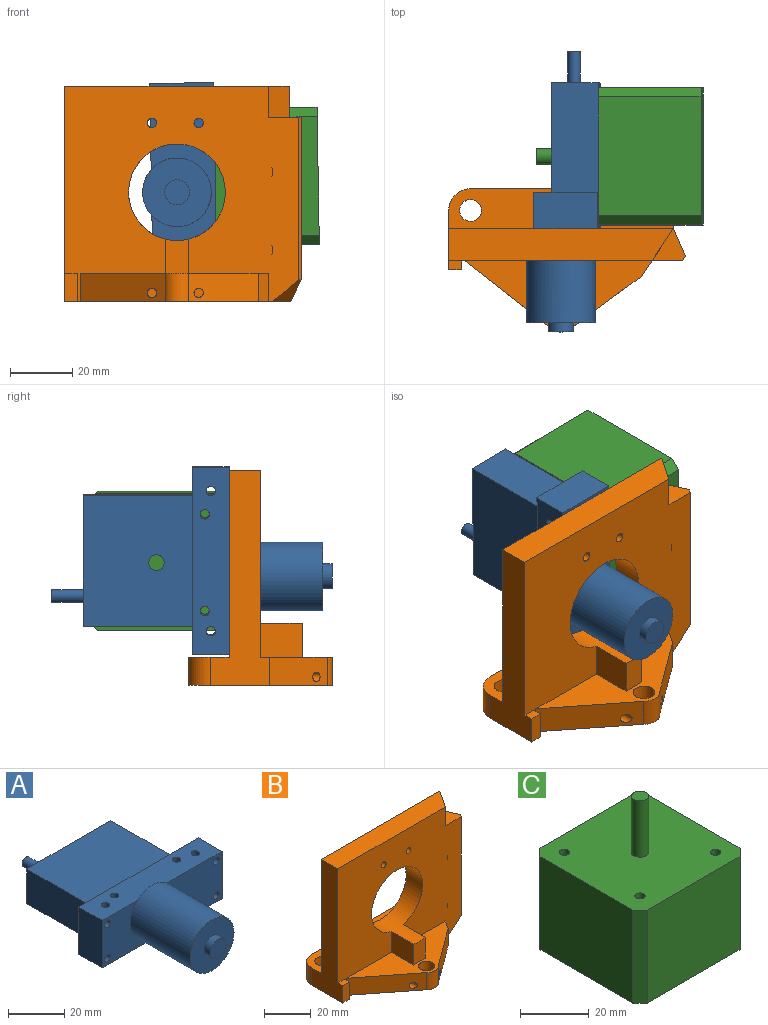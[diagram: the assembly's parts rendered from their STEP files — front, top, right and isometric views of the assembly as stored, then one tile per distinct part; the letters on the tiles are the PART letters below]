
ASSEMBLY  parts=3 mates=2
PART A: 25 faces, bbox 60x89.8x23.3 mm
  f0: plane 20.5x11.8mm, normal (1,0,0), area 241.9mm2, adj f1,f7,f8,f9
  f1: plane 60x20.5mm, normal (0,1,0), area 571.7mm2, adj f0,f2,f8,f9,f10,f11,f12,f13
  f2: plane 20.5x11.8mm, normal (-1,0,0), area 241.9mm2, adj f1,f7,f8,f9
  f3: cylinder r=1.5mm len=20.5mm, axis (0,0,-1), area 193.2mm2, adj f8,f9
  f4: cylinder r=1.5mm len=20.5mm, axis (0,0,-1), area 193.2mm2, adj f8,f9
  f5: cylinder r=1.5mm len=20.5mm, axis (0,0,-1), area 193.2mm2, adj f8,f9
  f6: cylinder r=1.5mm len=20.5mm, axis (0,0,-1), area 193.2mm2, adj f8,f9
  f7: plane 60x20.5mm, normal (0,-1,0), area 850.3mm2, adj f0,f2,f8,f9,f10,f11,f12,f13
  f8: plane 60x11.8mm, normal (0,0,1), area 679.7mm2, adj f0,f1,f2,f3,f4,f5,f6,f7
  f9: plane 60x46.8mm, normal (0,0,-1), area 2149.7mm2, adj f0,f1,f2,f3,f4,f5,f6,f7
  f10: cylinder r=1.5mm len=11.8mm, axis (0,1,0), area 111.2mm2, adj f1,f7
  f11: cylinder r=1.5mm len=11.8mm, axis (0,1,0), area 111.2mm2, adj f1,f7
  f12: cylinder r=1.5mm len=11.8mm, axis (0,1,0), area 111.2mm2, adj f1,f7
  f13: cylinder r=1.5mm len=11.8mm, axis (0,1,0), area 111.2mm2, adj f1,f7
  f14: plane 14.75x2.84mm, normal (0,1,0), area 28.7mm2, adj f8,f15
  f15: cylinder r=11mm len=30mm, axis (0,1,0), area 2073.5mm2, adj f7,f14,f16
  f16: plane 22x22mm, normal (0,-1,0), area 329.9mm2, adj f15,f17
  f17: cylinder r=4mm len=8mm, axis (0,1,0), area 75.4mm2, adj f16,f18
  f18: plane 8x8mm, normal (0,-1,0), area 50.3mm2, adj f17
  f19: plane 35x15mm, normal (1,0,0), area 525mm2, adj f1,f9,f21,f22
  f20: plane 35x15mm, normal (-1,0,0), area 525mm2, adj f1,f9,f21,f22
  f21: plane 42x35mm, normal (0,0,1), area 1470mm2, adj f1,f19,f20,f22
  f22: plane 42x15mm, normal (0,1,0), area 617.4mm2, adj f9,f19,f20,f21,f23
  f23: cylinder r=2mm len=10mm, axis (0,-1,0), area 125.7mm2, adj f22,f24
  f24: plane 4x4mm, normal (0,1,0), area 12.6mm2, adj f23
PART B: 47 faces, bbox 76.3x46.5x69.5 mm
  f0: plane 60.32x23mm, normal (0,0,1), area 624.9mm2, adj f1,f2,f11,f12,f13,f17,f35,f36
  f1: plane 75.19x69.19mm, normal (0,-1,0), area 3624.5mm2, adj f0,f2,f3,f8,f10,f11,f14,f19
  f2: plane 9x4.97mm, normal (0.83,-0.56,0), area 53.8mm2, adj f0,f1,f13,f19
  f3: plane 4x3mm, normal (0,0,1), area 12mm2, adj f1,f8,f9,f10
  f4: plane 72x13mm, normal (0,0,1), area 838mm2, adj f5,f6,f7,f8,f15,f16,f18,f25
  f5: cylinder r=7mm len=9mm, axis (0,0,-1), area 99mm2, adj f4,f6,f18,f19
  f6: plane 58x9mm, normal (0,1,0), area 522mm2, adj f4,f5,f7,f19
  f7: cylinder r=7mm len=9mm, axis (0,0,-1), area 99mm2, adj f4,f6,f8,f19
  f8: plane 69x19mm, normal (-1,0,0), area 771mm2, adj f1,f3,f4,f7,f9,f19,f25,f26
  f9: plane 9x4mm, normal (0,-1,0), area 36mm2, adj f3,f8,f10,f19
  f10: plane 9x3mm, normal (1,0,0), area 27mm2, adj f1,f3,f9,f19
  f11: plane 27.86x21.93mm, normal (-0.62,-0.79,0), area 303.8mm2, adj f0,f1,f12,f19,f39
  f12: cylinder r=5mm len=9mm, axis (0,0,-1), area 73.3mm2, adj f0,f11,f13,f19
  f13: plane 22.83x16.93mm, normal (0.59,-0.81,0), area 241.2mm2, adj f0,f2,f12,f19,f38
  f14: plane 10x10mm, normal (0.83,-0.56,0), area 120.3mm2, adj f1,f25,f26,f29
  f15: cylinder r=3.5mm len=9mm, axis (0,0,-1), area 197.9mm2, adj f4,f19
  f16: cylinder r=3.5mm len=9mm, axis (0,0,-1), area 197.9mm2, adj f4,f19
  f17: cylinder r=3.5mm len=9mm, axis (0,0,-1), area 197.9mm2, adj f0,f19
  f18: plane 9x6mm, normal (1,0,0), area 54mm2, adj f4,f5,f19,f28
  f19: plane 72.44x46mm, normal (0,0,-1), area 2030.2mm2, adj f1,f2,f5,f6,f7,f8,f9,f10
  f20: plane 30x5mm, normal (0,-1,0), area 135.9mm2, adj f19,f21,f23,f24,f40,f42
  f21: plane 8x5mm, normal (1,0,0), area 40mm2, adj f19,f20,f22,f24
  f22: plane 30x5mm, normal (0,1,0), area 135.9mm2, adj f19,f21,f23,f24,f38,f39
  f23: plane 8x5mm, normal (-1,0,0), area 40mm2, adj f19,f20,f22,f24
  f24: plane 30x8mm, normal (0,0,-1), area 240mm2, adj f20,f21,f22,f23
  f25: plane 72x60mm, normal (0,1,0), area 3551.1mm2, adj f4,f8,f14,f26,f28,f44,f45,f46
  f26: plane 72x10mm, normal (0,0,1), area 686.6mm2, adj f1,f8,f14,f25
  f27: plane 52x1.31mm, normal (0.84,-0.54,0), area 80.8mm2, adj f1,f28,f29,f30
  f28: plane 59x8.69mm, normal (0.91,0.4,0), area 491.8mm2, adj f18,f19,f25,f27,f29,f30,f31,f33
  f29: plane 10.52x10mm, normal (0,0,1), area 54.6mm2, adj f1,f14,f27,f28
  f30: plane 9.14x9mm, normal (0.6,-0.38,-0.71), area 60.5mm2, adj f1,f19,f27,f28
  f31: cylinder r=2.5mm len=10.25mm, axis (0.91,0.4,0), area 141.4mm2, adj f1,f28,f32
  f32: cone r=0mm half-angle=59deg, axis (0.91,0.4,0), area 22.9mm2, adj f1,f31
  f33: cylinder r=2.5mm len=10.25mm, axis (0.91,0.4,0), area 141.4mm2, adj f1,f28,f34
  f34: cone r=0mm half-angle=59deg, axis (0.91,0.4,0), area 22.9mm2, adj f1,f33
  f35: plane 13.46x10.93mm, normal (-1,0,0), area 147.1mm2, adj f0,f1,f37,f46
  f36: plane 13.46x10.93mm, normal (1,0,0), area 147.1mm2, adj f0,f1,f37,f46
  f37: plane 10.93x7.21mm, normal (0,-1,0), area 76.7mm2, adj f0,f35,f36,f46
  f38: cylinder r=1.5mm len=20.1mm, axis (0,1,0), area 179.4mm2, adj f13,f22
  f39: cylinder r=1.5mm len=19.16mm, axis (0,1,0), area 169.8mm2, adj f11,f22
  f40: cylinder r=1.5mm len=3mm, axis (0,1,0), area 18.8mm2, adj f20,f41
  f41: plane 3x3mm, normal (0,-1,0), area 7.1mm2, adj f40
  f42: cylinder r=1.5mm len=3mm, axis (0,1,0), area 18.8mm2, adj f20,f43
  f43: plane 3x3mm, normal (0,-1,0), area 7.1mm2, adj f42
  f44: cylinder r=1.5mm len=10mm, axis (0,1,0), area 94.2mm2, adj f1,f25
  f45: cylinder r=1.5mm len=10mm, axis (0,1,0), area 94.2mm2, adj f1,f25
  f46: cylinder r=15.5mm len=31mm, axis (0,1,0), area 1071.8mm2, adj f1,f25,f35,f36,f37
PART C: 20 faces, bbox 44x44x53 mm
  f0: plane 38x33mm, normal (1,0,0), area 1254mm2, adj f4,f5,f10,f11
  f1: plane 38x33mm, normal (0,1,0), area 1254mm2, adj f4,f5,f9,f11
  f2: plane 38x33mm, normal (-1,0,0), area 1254mm2, adj f4,f5,f8,f9
  f3: plane 38x33mm, normal (0,-1,0), area 1254mm2, adj f4,f5,f8,f10
  f4: plane 44x44mm, normal (0,0,1), area 1870.1mm2, adj f0,f1,f2,f3,f6,f8,f9,f10
  f5: plane 44x44mm, normal (0,0,-1), area 1918mm2, adj f0,f1,f2,f3,f8,f9,f10,f11
  f6: cylinder r=2.5mm len=20mm, axis (0,0,-1), area 314.2mm2, adj f4,f7
  f7: plane 5x5mm, normal (0,0,1), area 19.6mm2, adj f6
  f8: plane 33x3mm, normal (-0.71,-0.71,0), area 140mm2, adj f2,f3,f4,f5
  f9: plane 33x3mm, normal (-0.71,0.71,0), area 140mm2, adj f1,f2,f4,f5
  f10: plane 33x3mm, normal (0.71,-0.71,0), area 140mm2, adj f0,f3,f4,f5
  f11: plane 33x3mm, normal (0.71,0.71,0), area 140mm2, adj f0,f1,f4,f5
  f12: cylinder r=1.5mm len=10mm, axis (0,0,1), area 94.2mm2, adj f4,f13
  f13: plane 3x3mm, normal (0,0,1), area 7.1mm2, adj f12
  f14: cylinder r=1.5mm len=10mm, axis (0,0,1), area 94.2mm2, adj f4,f15
  f15: plane 3x3mm, normal (0,0,1), area 7.1mm2, adj f14
  f16: cylinder r=1.5mm len=10mm, axis (0,0,1), area 94.2mm2, adj f4,f17
  f17: plane 3x3mm, normal (0,0,1), area 7.1mm2, adj f16
  f18: cylinder r=1.5mm len=10mm, axis (0,0,1), area 94.2mm2, adj f4,f19
  f19: plane 3x3mm, normal (0,0,1), area 7.1mm2, adj f18
PLACE A rot(axis=(0,-1,0),91deg) t=(19.9,29.71,-42.74)mm
PLACE B t=(7.64,36.81,-82.95)mm fixed
PLACE C rot(axis=(0,-1,0),91deg) t=(52.9,47.11,-42.69)mm
MATE fastened C.f16 <-> A.f6  axis (-1,0,-0.02) through (19.64,31.61,-27.74)mm
MATE revolute B.f46 <-> A.f15  axis (0,1,0) through (7.64,23.81,-47.95)mm
